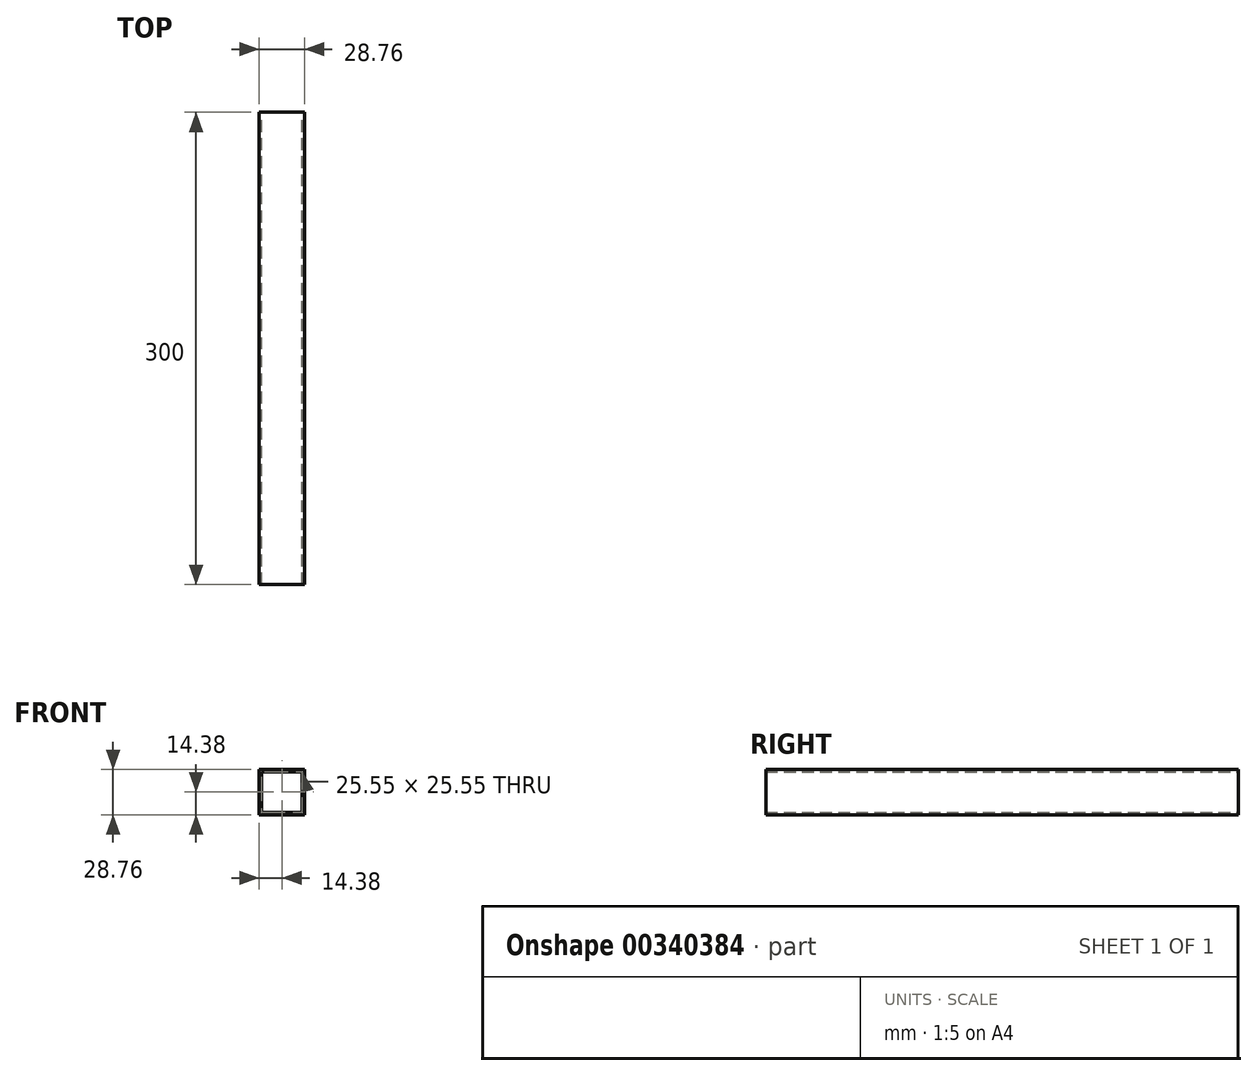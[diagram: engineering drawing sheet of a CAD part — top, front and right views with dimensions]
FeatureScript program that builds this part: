
annotation { "Feature Type Name" : "Feature", "Feature Type Description" : "" }
export const myFeature = defineFeature(function(context is Context, id is Id, definition is map)
    precondition{}
    {
        {
            var Q0;
            Q0=qCreatedBy(makeId("Front.planeOp"),FACE);
            var sketch = newSketch(context, id + "F0", { "sketchPlane" : qUnion([Q0])});
            skLineSegment(sketch, "E0.bottom", {"start": v(14.37, 14.38) * mm, "end": v(-14.38, 14.38) * mm});
            skLineSegment(sketch, "E0.top", {"start": v(14.38, -14.38) * mm, "end": v(-14.37, -14.38) * mm});
            skLineSegment(sketch, "E0.left", {"start": v(14.37, 14.37) * mm, "end": v(14.38, -14.38) * mm});
            skLineSegment(sketch, "E0.right", {"start": v(-14.38, 14.38) * mm, "end": v(-14.37, -14.38) * mm});
            skPoint(sketch, "E0.middle", {"position": v(0, 0) * mm});
            skSolve(sketch);
        }
        {
            var Q0;
            Q0 = qSketchRegion(id + "F0", true);
            extrude(context, id + "F1", {"entities" : qUnion([Q0]), "depth" : 300 * mm});
        }
        {
            var Q0;
            Q0=makeQuery(id+"F1.opExtrude","CAP_FACE",FACE,{"disambiguationData":[OSD([sQuery(id+"F0.wireOp",EDGE,"E0.bottom"),sQuery(id+"F0.wireOp",EDGE,"E0.top"),sQuery(id+"F0.wireOp",EDGE,"E0.left"),sQuery(id+"F0.wireOp",EDGE,"E0.right")])],"isStart":true});
            var Q1;
            Q1=makeQuery(id+"F1.opExtrude","CAP_FACE",FACE,{"disambiguationData":[OSD([sQuery(id+"F0.wireOp",EDGE,"E0.bottom"),sQuery(id+"F0.wireOp",EDGE,"E0.top"),sQuery(id+"F0.wireOp",EDGE,"E0.left"),sQuery(id+"F0.wireOp",EDGE,"E0.right")])],"isStart":false});
            var Q2;
            Q2=makeQuery(id+"F1.opExtrude","SWEPT_BODY",BODY,{"disambiguationData":[OSD([sQuery(id+"F0.wireOp",EDGE,"E0.bottom"),sQuery(id+"F0.wireOp",EDGE,"E0.top"),sQuery(id+"F0.wireOp",EDGE,"E0.left"),sQuery(id+"F0.wireOp",EDGE,"E0.right")])]});
            shell(context, id + "F2", {"entities" : qUnion([Q0, Q1]), "parts" : qUnion([Q2]), "thickness" : 1.6 * mm});
        }
    });
